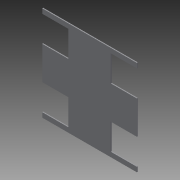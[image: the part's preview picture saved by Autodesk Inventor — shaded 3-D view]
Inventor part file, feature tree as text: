
AUTODESK INVENTOR PART (.ipt)
format: ipt  version: 2014 (Build 180170000, 170)  size: 94,208 bytes
history: native  units: mm
features: extrude x1, sketch x1
ambient origin geometry x8: Origin, YZ Plane, XZ Plane, XY Plane, X Axis, Y Axis, Z Axis, Center Point
bodies: Volumenkörper1 (feature_tree)
feature tree (2):
  extrude  "Extrusion1"  Depth=110.0mm
  sketch  "Skizze1"  dims[d17=180.0mm d19=110.0mm d20=110.0mm d23=140.0mm d25=20.0mm d26=4.0mm d27=0.0mm]
